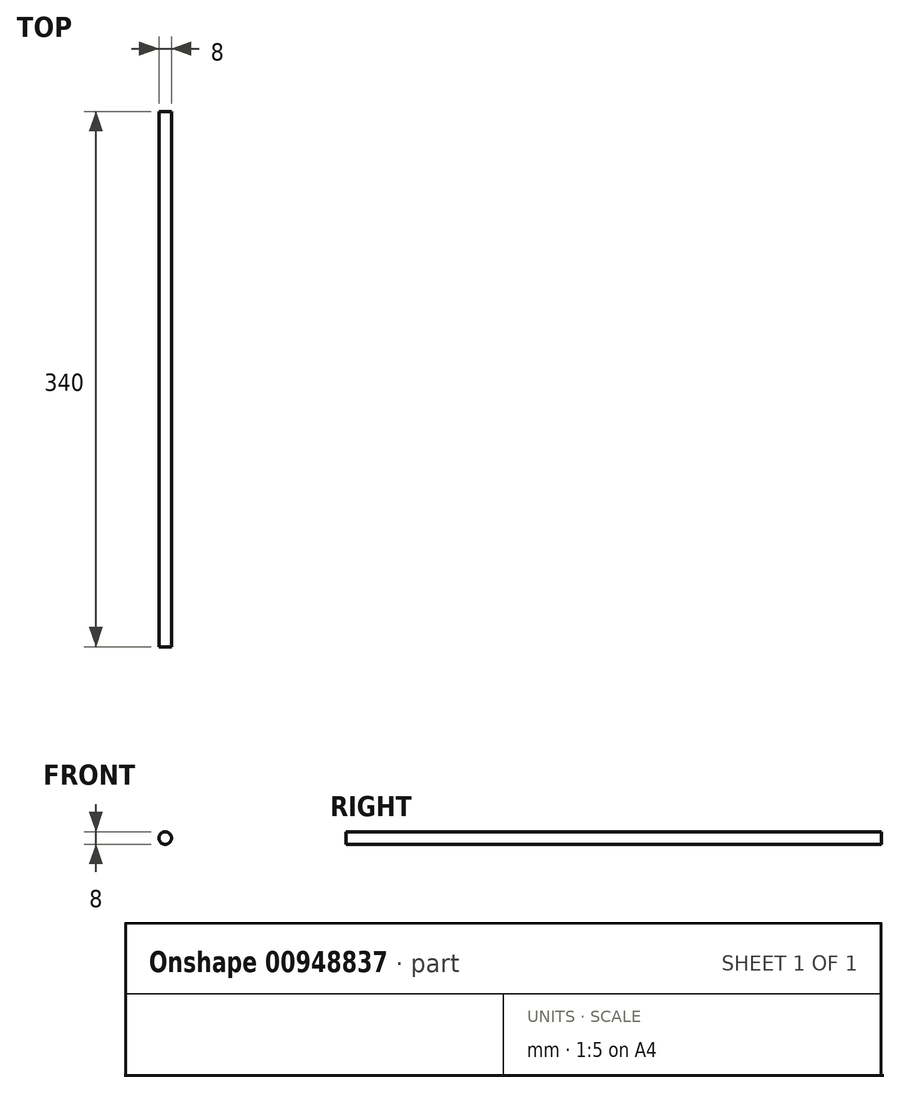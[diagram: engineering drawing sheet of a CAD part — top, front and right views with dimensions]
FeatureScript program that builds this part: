
annotation { "Feature Type Name" : "Feature", "Feature Type Description" : "" }
export const myFeature = defineFeature(function(context is Context, id is Id, definition is map)
    precondition{}
    {
        {
            var Q0;
            Q0=qCreatedBy(makeId("Front.planeOp"),FACE);
            var sketch = newSketch(context, id + "F0", { "sketchPlane" : qUnion([Q0])});
            skCircle(sketch, "E0", {"center": v(0, 0) * mm, "radius": 4 * mm});
            skSolve(sketch);
        }
        {
            var Q0;
            Q0=qSketchRegion(id+"F0",true);
            extrude(context, id + "F1", {"entities" : qUnion([Q0]), "depth" : 340 * mm, "offsetDistance" : 25 * mm});
        }
    });
